# Revit family: QF_ELECTROLUXPROFESSIONAL_169105_ACFG24
name_source: partatom
category: Specialty Equipment
revit_build: Autodesk Revit 2018 (Build: 20190510_1515(x64)
units: mm (PartAtom-declared; Revit-internal decimal feet)

## family parameters
Always vertical = Yes
Cut with Voids When Loaded = No
Part Type = Normal
Room Calculation Point = No
Round Connector Dimension = Use Diameter
Shared = Yes
Work Plane-Based = No

## types (1)
- QF_ELECTROLUXPROFESSIONAL_169105_ACFG24
    Description = 4 Open Gas Burner Range with Static Oven 24"
    Direct Waste Size = 0"
    Gas Input = 164000.0 Btu/h
    Gas KW = 48
    Gas Size = 1"
    HP = 0 HP
    Manufacturer = ELECTROLUX
    Model = ACFG24
    URL = www.electrolux.com/foodservice
    URL Cutsheet = www.electrolux.com/foodservice
    URL Manufacturer = www.electrolux.com/foodservice
    Watts = 0 W
    Weight = 282 lbs.

## geometry (parser evidence)
native form markers: Blend x23, Sweep x2
no freeform markers — native parametric forms only
